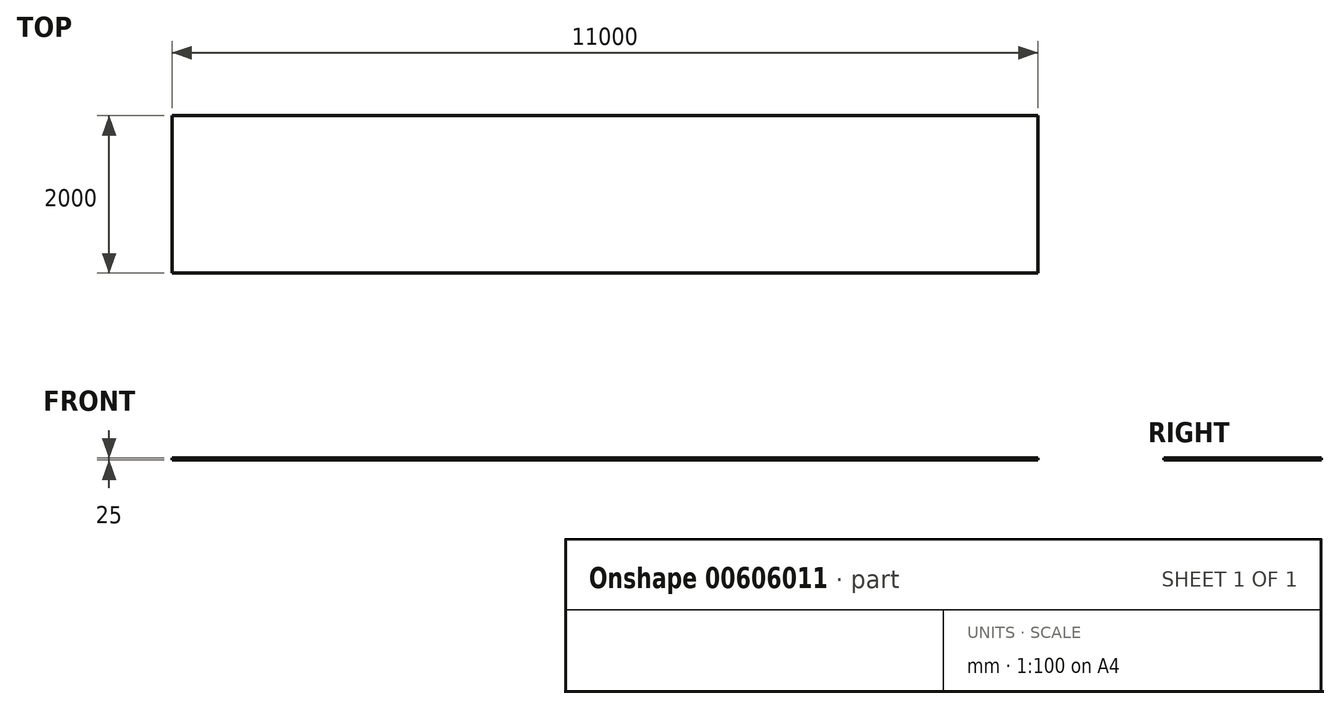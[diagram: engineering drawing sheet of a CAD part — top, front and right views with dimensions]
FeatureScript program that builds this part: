
annotation { "Feature Type Name" : "Feature", "Feature Type Description" : "" }
export const myFeature = defineFeature(function(context is Context, id is Id, definition is map)
    precondition{}
    {
        {
            var Q0;
            Q0=qCreatedBy(makeId("Top.planeOp"),FACE);
            var sketch = newSketch(context, id + "F0", { "sketchPlane" : qUnion([Q0])});
            skLineSegment(sketch, "E0.bottom", {"start": v(5500, -1000) * mm, "end": v(-5500, -1000) * mm});
            skLineSegment(sketch, "E0.top", {"start": v(5500, 1000) * mm, "end": v(-5500, 1000) * mm});
            skLineSegment(sketch, "E0.left", {"start": v(5500, -1000) * mm, "end": v(5500, 1000) * mm});
            skLineSegment(sketch, "E0.right", {"start": v(-5500, -1000) * mm, "end": v(-5500, 1000) * mm});
            skPoint(sketch, "E0.middle", {"position": v(0, 0) * mm});
            skSolve(sketch);
        }
        {
            var Q0;
            Q0=makeQuery(id+"F0.imprint","IMPRINT",FACE,{"disambiguationData":[TD([[makeQuery(id+"F0.imprint","IMPRINT",EDGE,{"derivedFrom":sQuery(id+"F0.wireOp",EDGE,"E0.bottom")}),-1.0]])]});
            extrude(context, id + "F1", {"entities" : qUnion([Q0]), "depth" : 25 * mm, "offsetDistance" : 25 * mm});
        }
    });
